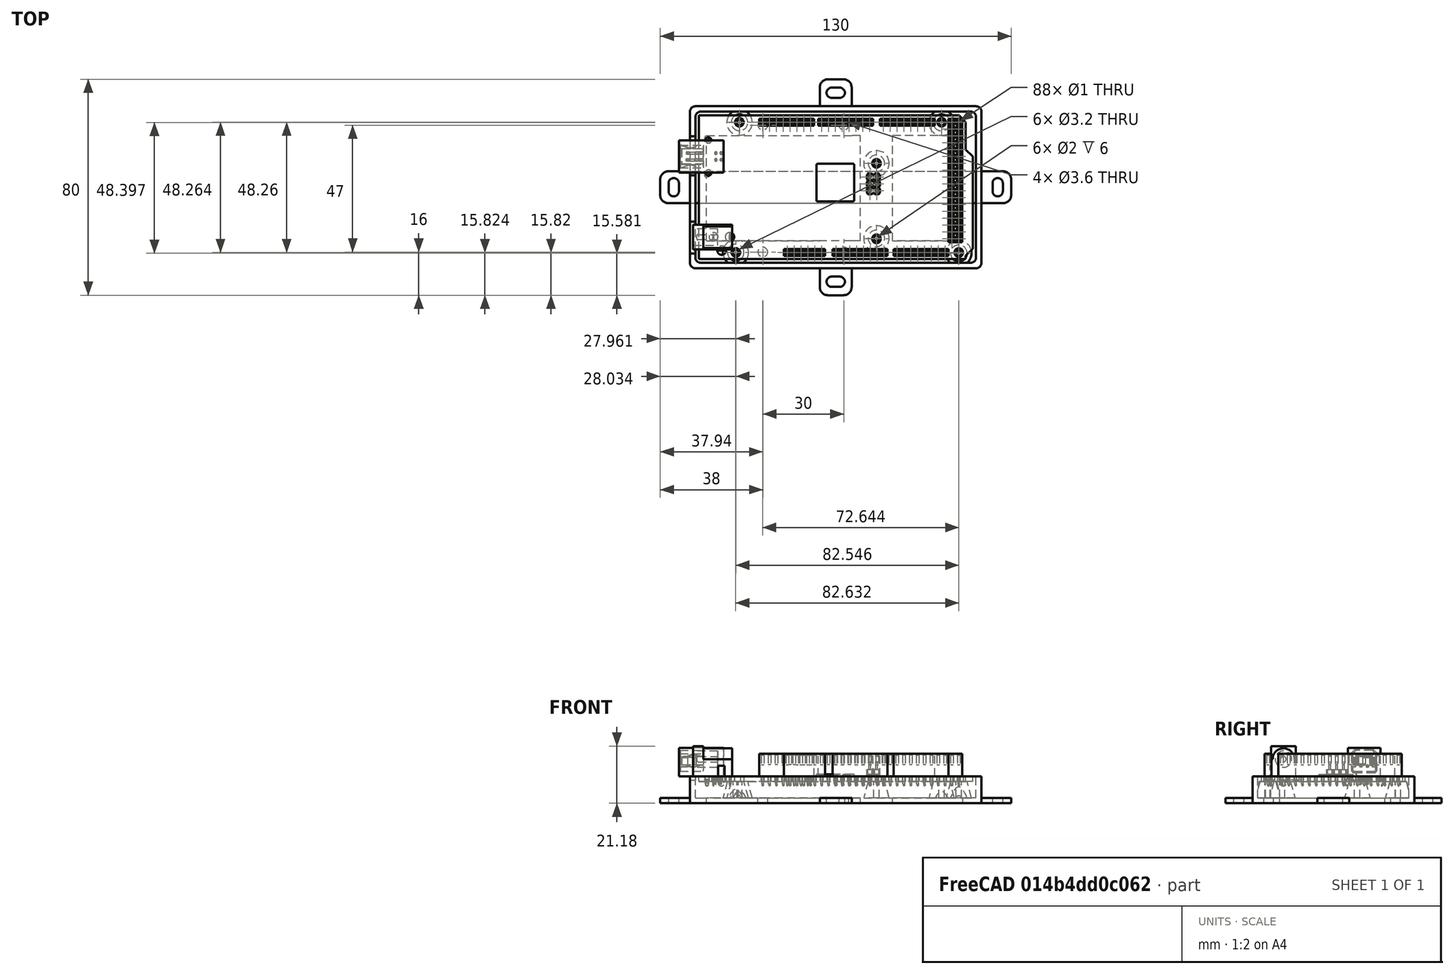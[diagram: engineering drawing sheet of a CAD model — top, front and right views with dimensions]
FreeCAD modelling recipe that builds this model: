
FCSTD DOCUMENT  (FreeCAD 0.19R23578 (Git))
Label: arduino_mega
License: All rights reserved
LicenseURL: http://en.wikipedia.org/wiki/All_rights_reserved
objects: Part::FeaturePython×8, Part::Box×6, Part::Feature×3, Part::MultiFuse×3, Part::Cut×3, Part::Cylinder×2, Part::Fillet×2, Part::Cone×1, Spreadsheet::Sheet×1, Part::Compound×1
note: 29 computed .brp shape members not serialized (recipe doc carries the construction recipe); baked Part::Feature solids carry a one-line shape summary decoded from their .brp

FEATURE [Part::Feature] Compound009001  label="Arduino-mega mockup"
  Placement = pos=(54,30,8) rot=(0,0,1;0rad)
  shape: bbox 108.8 x 53.17 x 14.81 mm, 2108 faces, 108 solids (baked)
FEATURE [Part::Cone] Cone
  Angle = 360
  AttacherType = Attacher::AttachEngine3D
  Height = 7
  Radius1 = 5
  Radius2 = 3.05
FEATURE [Part::Cylinder] Cylinder001  label="screw hole001"
  Angle = 360
  AttacherType = Attacher::AttachEngine3D
  Height = 20
  Radius = 1.8
FEATURE [Part::FeaturePython] Array001  label="screw hole array001"  # Draft array (typed FeaturePython)
  Angle = 360
  ArrayType = 0
  Axis = (0,0,1)
  Base = -> Cylinder001
  Center = (0,0,0)
  Fuse = false
  IntervalAxis = (0,0,0)
  IntervalX = (30,0,0)
  IntervalY = (0,47,0)
  IntervalZ = (0,0,1)
  NumberPolar = 1
  NumberX = 2
  NumberY = 2
  NumberZ = 1
  Placement = pos=(27,6,-5) rot=(0,0,1;0rad)
  expr: .Placement.Base.y = <<p>>.box_tube_connector_hole_y_off
  expr: .Placement.Base.x = <<p>>.box_tube_connector_hole_x_off + 22
  expr: .IntervalY.y = <<p>>.box_tube_connector_hole_y_dist
  expr: .IntervalX.x = <<p>>.box_tube_connector_hole_x_dist
FEATURE [Part::Box] cube003  label="usb hole cube"
  AttacherType = Attacher::AttachEngine3D
  Height = 15
  Length = 2.6
  Placement = pos=(-0.5,34.4,8.6) rot=(0,0,1;0rad)
  Width = 14.43
FEATURE [Part::Box] cube
  AttacherType = Attacher::AttachEngine3D
  Height = 10
  Length = 108
  Width = 60
FEATURE [Part::Fillet] Fillet001
  Base = -> cube
  Edges = 4 edges r=2: [Edge1,Edge3,Edge5,Edge7]
FEATURE [Part::Box] cube001  label="extraction cube"
  AttacherType = Attacher::AttachEngine3D
  Height = 16
  Length = 104
  Placement = pos=(2,2,2) rot=(0,0,1;0rad)
  Width = 56
FEATURE [Part::Fillet] Fillet002
  Base = -> cube001
  Edges = 4 edges r=2: [Edge1,Edge3,Edge5,Edge7]
FEATURE [Part::Box] cube002  label="power hole cube"
  AttacherType = Attacher::AttachEngine3D
  Height = 15
  Length = 2.6
  Placement = pos=(-0.5,5.4,8.6) rot=(0,0,1;0rad)
  Width = 11.89
FEATURE [Part::MultiFuse] union
  Shapes = -> [cube002,cube003,Fillet002]
FEATURE [Spreadsheet::Sheet] Spreadsheet  label="p"
  cells = A1=hole_r; B1(hole_r)=1; A2=box_tube_connector_hole_x_dist; B2(box_tube_connector_hole_x_dist)=30; A3=box_tube_connector_hole_y_dist; B3(box_tube_connector_hole_y_dist)=47; A4=box_tube_connector_hole_y_off; B4(box_tube_connector_hole_y_off)=6; A5=box_tube_connector_hole_x_off; B5(box_tube_connector_hole_x_off)=5; A7=attach_hole_dist; B7(attach_hole_dist)=10; A8=attach_hole_r; B8(attach_hole_r)=1.9
FEATURE [Part::Box] cube006  label="central hole cube"
  AttacherType = Attacher::AttachEngine3D
  Height = 17
  Length = 57
  Placement = pos=(6.1,10.1,0) rot=(0,0,1;0rad)
  Width = 39
FEATURE [Part::Cylinder] cylinder009
  Angle = 360
  AttacherType = Attacher::AttachEngine3D
  Height = 8
  Radius = 1
  expr: Radius = <<p>>.hole_r
FEATURE [Part::Cut] difference003  label="hole with stand"
  Base = -> Cone
  Placement = pos=(13.97,2.54,0) rot=(0,0,1;0rad)
  Tool = -> cylinder009
FEATURE [Part::Cut] difference
  Base = -> Fillet001
  Tool = -> union
FEATURE [Part::FeaturePython] Point004  # WARN: FeaturePython — macro-defined, semantics opaque (R4)
  Placement = pos=(99.6224,5.54123,0) rot=(0,0,1;0rad)
  X = 99.6224
  Y = 5.54123
  Z = 0
FEATURE [Part::FeaturePython] Point005  # WARN: FeaturePython — macro-defined, semantics opaque (R4)
  Placement = pos=(93.2501,53.8816,0) rot=(0,0,1;0rad)
  X = 93.2501
  Y = 53.8816
  Z = 0
FEATURE [Part::FeaturePython] Point  # WARN: FeaturePython — macro-defined, semantics opaque (R4)
  Placement = pos=(69.112,38.8,0) rot=(0,0,1;0rad)
  X = 69.112
  Y = 38.8
  Z = 0
FEATURE [Part::FeaturePython] Point006  # WARN: FeaturePython — macro-defined, semantics opaque (R4)
  Placement = pos=(69.1,11,0) rot=(0,0,1;0rad)
  X = 69.1
  Y = 11
  Z = 0
FEATURE [Part::FeaturePython] Point007  # WARN: FeaturePython — macro-defined, semantics opaque (R4)
  Placement = pos=(16.9906,5.80847,0) rot=(0,0,1;0rad)
  X = 16.9906
  Y = 5.80847
  Z = 0
FEATURE [Part::FeaturePython] Point008  # WARN: FeaturePython — macro-defined, semantics opaque (R4)
  Placement = pos=(18.3986,53.9385,0) rot=(0,0,1;0rad)
  X = 18.3986
  Y = 53.9385
  Z = 0
FEATURE [Part::Compound] Compound
  Links = -> [Point004,Point005,Point,Point006,Point007,Point008]
FEATURE [Part::FeaturePython] PointArray  label="hole point array"  # Draft array (typed FeaturePython)
  Base = -> difference003
  Count = 4
  ExtraPlacement = pos=(13.97,2.54,0) rot=(0,0,1;0rad)
  Placement = pos=(-14,-2.5,1) rot=(0,0,1;0rad)
  PointObject = -> Compound
FEATURE [Part::Box] cube007  label="central hole cube001"
  AttacherType = Attacher::AttachEngine3D
  Height = 17
  Length = 26
  Placement = pos=(75.1,10.1,0) rot=(0,0,1;0rad)
  Width = 39
FEATURE [Part::MultiFuse] Fusion001  label="arduino box extraction fusion"
  Shapes = -> [Array001,cube006,cube007]
FEATURE [Part::Feature] Cut003002  label="attach plane y dir002"
  Placement = pos=(48.1,-10,0) rot=(0,0,1;0rad)
  shape: bbox 11.8 x 80 x 2 mm, 20 faces (baked)
FEATURE [Part::MultiFuse] union003  label="body fusion"
  Shapes = -> [difference,PointArray,Cut003002]
FEATURE [Part::Cut] difference007  label="arduino mega box cut"
  Base = -> union003
  Tool = -> Fusion001
FEATURE [Part::Feature] Cut003001  label="attach plane x dir001"
  Placement = pos=(-11,24.1,0) rot=(0,0,1;0rad)
  shape: bbox 130 x 11.8 x 2 mm, 18 faces (baked)
